# Revit family: 201_RONDO-_+VAL
name_source: partatom
category: Air Terminals
units: mm (PartAtom-declared; Revit-internal decimal feet)

## family parameters
Always vertical = Yes
Cut with Voids When Loaded = No
Part Type = Normal
Room Calculation Point = Yes
Round Connector Dimension = Use Diameter
Shared = No
Work Plane-Based = No

## types (1)
- RONDO-125+VAL
    C = 115 mm  [stored 0.377297 ft]
    C1 = 110 mm  [stored 0.360892 ft]
    CAT0 = Yes
    CLBTZ = 0 mm  [stored 0 ft]
    CLD = 125 mm  [stored 0.410105 ft]
    CLD1 = 63 mm
    CL_Location_5000 = 5000 mm  [stored 16.4042 ft]
    D = 125 mm
    D21 = 122 mm
    D22 = 102 mm
    Description = Air diffuser with plenum sound attenuator
    H1 = 2 mm  [stored 0.00656168 ft]
    H2 = 171 mm  [stored 0.561024 ft]
    H3 = 173 mm  [stored 0.567585 ft]
    H4 = 23 mm  [stored 0.0754593 ft]
    H5 = 75 mm
    H_ARR = 0 mm  [stored 0 ft]
    L1 = 215 mm  [stored 0.705381 ft]
    L2 = 210 mm  [stored 0.688976 ft]
    L_ARR = 400 mm  [stored 1.31234 ft]
    M1 = 115 mm  [stored 0.377297 ft]
    M2 = 108 mm  [stored 0.354331 ft]
    M3 = 110 mm  [stored 0.360892 ft]
    MC_Default_elevation = 0 mm  [stored 0 ft]
    Manufacturer = Climecon
    QmdConnectorList = 201;D
    URL = www.climecon.fi
    W1 = 2 mm  [stored 0.00656168 ft]
    W1__ve = -2 mm  [stored -0.00656168 ft]
    W_ARR = 400 mm  [stored 1.31234 ft]
    XRefLineVPlnId = 7453
    YRefLineVPlnId = 7456
    magiPartTypeId = 201
    magiProductCode = RONDO-125+VAL
    magiProductFamilyId = RONDO-*+VAL
    magiProductId = RONDO-125+VAL

note: [stored X ft] marks values corroborated as IEEE doubles in the binary element streams (Revit-internal decimal feet)

## geometry (parser evidence)
native form markers: Sweep x1
no freeform markers — native parametric forms only
